# Revit family: PCR-23
name_source: partatom
category: Air Terminals
revit_build: Autodesk Revit MEP 2012 (Build: 20110309_2315(x64)
units: mm (PartAtom-declared; Revit-internal decimal feet)

## types (7) — shared parameters
Cuello Especial Cuadrado = 15"x15"
Cuello Min-Max Cuadrado = 6"x6" a 15"x15" en Incrementos de 2"
Cuello Min-Max Redondo = 6" hasta 16" en Incrementos de 2"
Description = Difusor perforado para Retorno
Función = Retorno
Manufacturer = INNES
Material = Aluminio/Acero
Model = PCR
Nota1//Redondo = .
Nota2//Cuadrado = .
Posición de Instalación = Techo
Tipo de Cuello = Redondo/Cuadrado
Type Comments = Malla perforada desmontable
URL = https://www.innes.com.mx
Visible_Texto1 = No
Visible_Texto2 = No
Visible_Texto_SCuello = No

## per-type parameters (varying)
| type | Conect_Cuadrado | Conect_Redondo | Medida_Requerida | Nota_SCuello | Redondo(1)Cuadrado(2) | Seleccion_Cuello | Var1 | Var2 | Var3 | Visible_Conect_C | Visible_Conect_R |
| PCR-06-24 | 5 7/8" | 2 15/16" | 6" | Cuello Redondo | 1 | 1 | 6 | 6" | 6" | No | Yes |
| PCR-08-24 | 7 7/8" | 3 15/16" | 8" | Cuello Redondo | 1 | 1 | 8 | 8" | 8" | No | Yes |
| PCR-10-24 | 9 7/8" | 4 15/16" | 10" | Cuello Redondo | 1 | 1 | 10 | 10" | 10" | No | Yes |
| PCR-12-24 | 11 7/8" | 5 15/16" | 12" | Cuello Redondo | 1 | 1 | 12 | 12" | 12" | No | Yes |
| PCR-14-24 | 13 7/8" | 6 15/16" | 14" | Cuello cuadrado | 2 | 2 | 14 | 14" | 14" | Yes | No |
| PCR-15-24 Solo C.Cuadrado | 14 7/8" | 7 15/16" | 15" | Cuello cuadrado | 2 | 2 | 16 | 16" | 15" | Yes | No |
| PCR-16-24 | 14 7/8" | 7 15/16" | 16" | Cuello Redondo | 1 | 1 | 16 | 16" | 15" | No | Yes |

## geometry (parser evidence)
native form markers: Blend x14, Sweep x13
no freeform markers — native parametric forms only
